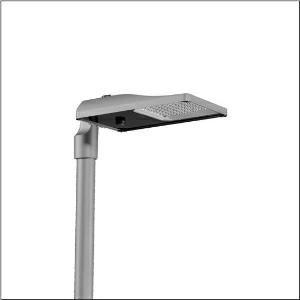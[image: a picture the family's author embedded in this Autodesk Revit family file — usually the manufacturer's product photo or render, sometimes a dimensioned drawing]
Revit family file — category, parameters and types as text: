
# Revit family: streetlight_sl_31_midi___pl52_5xh7h31t08la_6225
name_source: partatom
category: Lighting Fixtures
units: mm (PartAtom-declared; Revit-internal decimal feet)

## family parameters
Cut with Voids When Loaded = No
Host = Face
Light Source = No
Part Type = Normal
Room Calculation Point = No
Round Connector Dimension = Use Diameter
Shared = No

## types (1)
- --- (1 x LED, 12940 lm, 86.5 W, 3000K)
    Apparent Load = 87 VA
    CIE Flux Codes = 27 59 98 100 100
    Color Rendering = 70
    Color Temperature = 3000K
    Default Elevation = 1800 mm
    Description = Streetlight SL 31 midi D4i, Desk-Remote mast luminaire for post-top, side-entry; light control with lens of PMMA; light distribution: PL52, direct asymmetric distribution, for standard-compliant lighting for roads and squares; LED: luminous flux: 12.940lm, light colour: 730, colour temperature: 3000K; luminous efficacy: 149,6lm/W; control: pre-setting: logarithmic dimming characteristic, flexible luminous flux parameterisation, time-dependent luminous flux control, constant luminous flux control, power reduction, intelligent temperature release in ECG and LED module, overheat protection; luminaire housing, of diecast aluminium, SITECO metallic grey (DB 702S), corrosivity category C5 high according to DIN EN ISO 12944; cover of toughened safety glass, transparent, opened without tools; mast flange of diecast aluminium, SITECO metallic grey (DB 702S), spigot size: 76/60mm, mast flange included unmounted; cable length: 10,5m, connection cable pre-assembled; mains connection: 220..240V, AC, 50/60Hz; power consumption (at start of service life): 86,5W / (at end of service life): 90W / (with reduced operation 50%): 39,6W; protection rating (complete): IP66; insulation class (complete): insulation class II (safety insulation); impact resistance: IK09; certification: CE, ENEC, ENEC+, VDE, UKCA, ZD4i; permissible operating ambient temperature for outdoor applications: -40..+50°C; packaging unit: 1 piece

Light Distribution: PL52
    Height = 79 mm
    Lamp = 1 x LED
    Lamp Light Flux = 12940 lm
    Lamp Power = 86.5 W
    Lamp count = 1
    Length = 577 mm
    Luminous efficacy = 150 lm/W
    Manufacturer = Siteco
    ModVariant = No
    Model = 5XH7H31T08LA
    Mounting Place = Pole
    Mounting Type = Pole top
    Number of Poles = 1
    OnlyDefault = Yes
    Power Factor = 1
    Product Name = Streetlight SL 31 midi | PL52
    Product group = mast luminaire | pylon top
    ProductGroupID = 6100
    Protection Class = Protection class II
    Protection Degree = IP 66
    RLX_Detail_Level = 1
    RLX_Emergency_Light_Flux = 0 lm
    RLX_Emergency_Type = 0
    RLX_Emergency_Type_DB = No
    RlxData = <blob elided: 52413 chars, md5=9390cff5>
    Socket = socket
    Standby Power = 0 W
    System Light Flux = 12940 lm
    System Power = 87 W
    Type Comments = factory setting: luminous flux: 100 % | dim-lin: 254 | 456 mA
    Type Image = l_1300321.jpg
    URL = http://relux.com
    VarID = @adj_065797
    Voltage = 0 V
    Weight = 0.00 kg
    Width = 362 mm

## geometry (parser evidence)
native form markers: Blend x4, Sweep x10
no freeform markers — native parametric forms only
